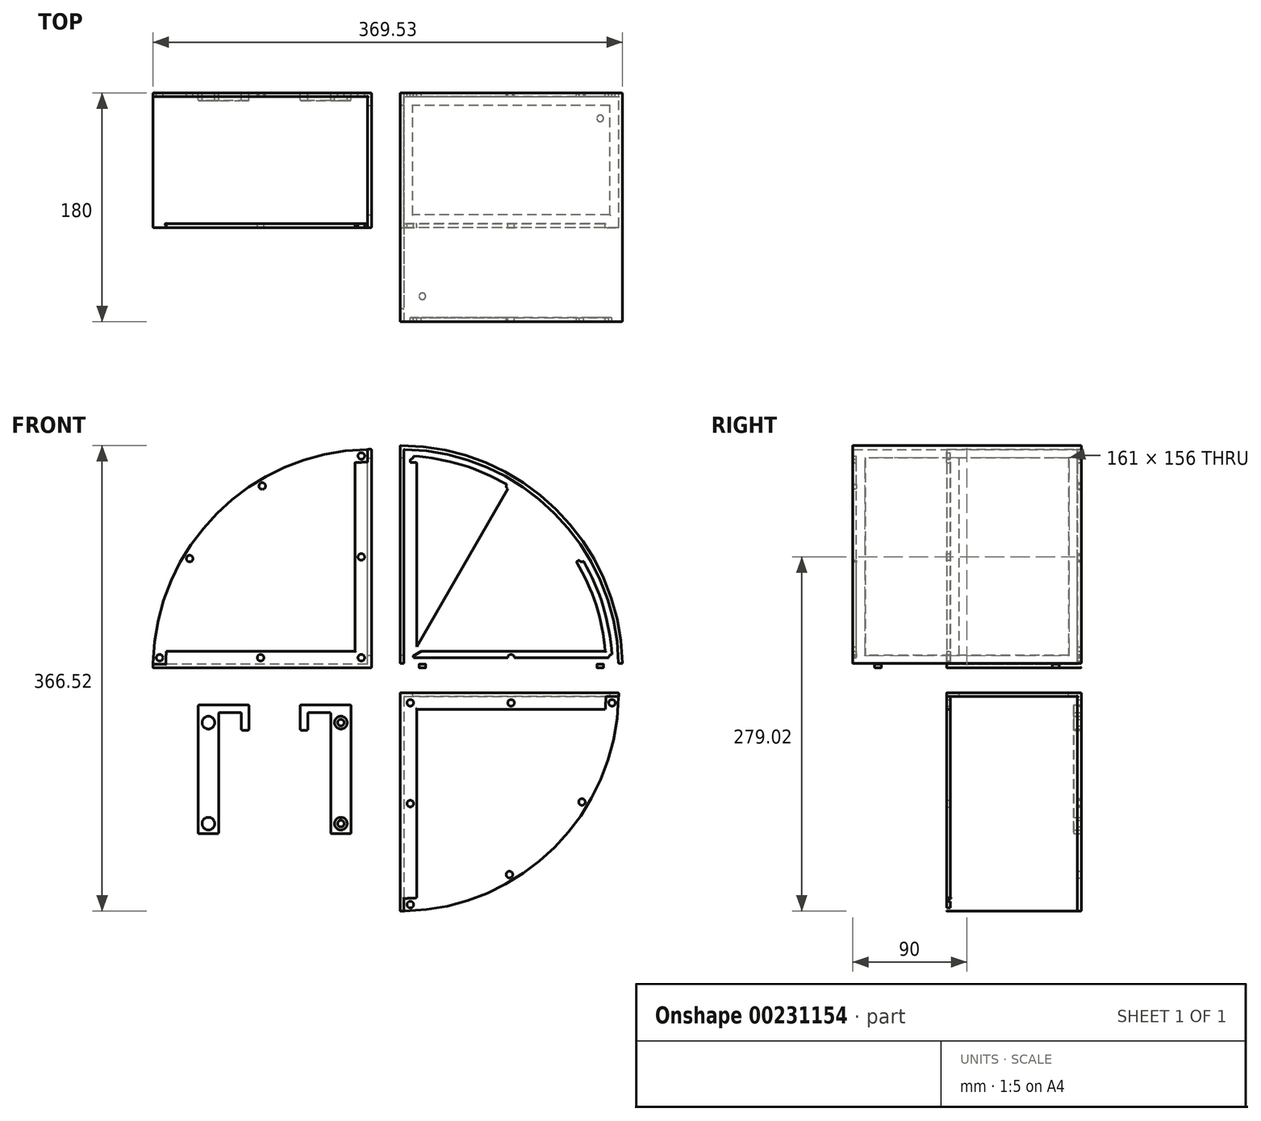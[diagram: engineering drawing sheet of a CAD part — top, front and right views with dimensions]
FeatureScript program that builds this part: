
annotation { "Feature Type Name" : "Feature", "Feature Type Description" : "" }
export const myFeature = defineFeature(function(context is Context, id is Id, definition is map)
    precondition{}
    {
        {
            var Q0;
            Q0=qCreatedBy(makeId("Front.planeOp"),FACE);
            var sketch = newSketch(context, id + "F0", { "sketchPlane" : qUnion([Q0])});
            skArc(sketch, "E0", {"start": v(186.3, 9.76) * mm, "mid": v(135.03, 133.5) * mm, "end": v(11.3, 184.76) * mm});
            skLineSegment(sketch, "E1", {"start": v(11.3, 184.76) * mm, "end": v(11.3, 9.76) * mm});
            skLineSegment(sketch, "E2", {"start": v(186.3, 9.76) * mm, "end": v(11.3, 9.76) * mm});
            skArc(sketch, "E3", {"start": v(11.3, 181.76) * mm, "mid": v(132.91, 131.38) * mm, "end": v(183.3, 9.76) * mm});
            skArc(sketch, "E4", {"start": v(11.3, 171.76) * mm, "mid": v(125.84, 124.31) * mm, "end": v(173.3, 9.76) * mm});
            skLineSegment(sketch, "E5", {"start": v(24.3, 22.76) * mm, "end": v(24.3, 171.24) * mm});
            skLineSegment(sketch, "E6", {"start": v(24.3, 171.24) * mm, "end": v(24.3, 22.76) * mm});
            skLineSegment(sketch, "E7", {"start": v(172.77, 22.76) * mm, "end": v(24.3, 22.76) * mm});
            skLineSegment(sketch, "E8", {"start": v(14.3, 12.76) * mm, "end": v(14.3, 181.73) * mm});
            skLineSegment(sketch, "E9", {"start": v(14.3, 12.76) * mm, "end": v(183.26, 12.76) * mm});
            skCircle(sketch, "E10", {"center": v(19.3, 17.76) * mm, "radius": 2.6 * mm});
            skArc(sketch, "E11", {"start": v(11.3, 176.76) * mm, "mid": v(129.38, 127.85) * mm, "end": v(178.3, 9.76) * mm});
            skCircle(sketch, "E12", {"center": v(19.3, 176.57) * mm, "radius": 2.6 * mm});
            skCircle(sketch, "E13", {"center": v(19.3, 97.07) * mm, "radius": 2.6 * mm});
            skCircle(sketch, "E14", {"center": v(98.6, 17.76) * mm, "radius": 2.6 * mm});
            skCircle(sketch, "E15", {"center": v(178.1, 17.76) * mm, "radius": 2.6 * mm});
            skCircle(sketch, "E16", {"center": v(97.31, 152.9) * mm, "radius": 2.6 * mm});
            skCircle(sketch, "E17", {"center": v(154.43, 95.78) * mm, "radius": 2.6 * mm});
            skLineSegment(sketch, "E18", {"start": v(19.3, 17.76) * mm, "end": v(19.3, 176.57) * mm});
            skLineSegment(sketch, "E19", {"start": v(19.3, 17.76) * mm, "end": v(178.1, 17.76) * mm});
            skLineSegment(sketch, "E20", {"start": v(19.3, 17.76) * mm, "end": v(97.31, 152.9) * mm});
            skLineSegment(sketch, "E21", {"start": v(19.3, 17.76) * mm, "end": v(154.43, 95.78) * mm});
            skLineSegment(sketch, "E22", {"start": v(0, 75.02) * mm, "end": v(0, -75.22) * mm});
            skLineSegment(sketch, "E23", {"start": v(-75, 0) * mm, "end": v(75.52, 0) * mm});
            skLineSegment(sketch, "E24.MirrorCS", {"start": v(186.3, -9.76) * mm, "end": v(11.3, -9.76) * mm});
            skLineSegment(sketch, "E25.MirrorCS", {"start": v(11.3, -184.76) * mm, "end": v(11.3, -9.76) * mm});
            skArc(sketch, "E26.MirrorCS", {"start": v(186.3, -9.76) * mm, "mid": v(135.03, -133.5) * mm, "end": v(11.3, -184.76) * mm});
            skArc(sketch, "E27.MirrorCS", {"start": v(11.3, -181.76) * mm, "mid": v(132.91, -131.38) * mm, "end": v(183.3, -9.76) * mm});
            skLineSegment(sketch, "E28.MirrorCS", {"start": v(14.3, -12.76) * mm, "end": v(14.3, -181.73) * mm});
            skLineSegment(sketch, "E29.MirrorCS", {"start": v(14.3, -12.76) * mm, "end": v(183.26, -12.76) * mm});
            skLineSegment(sketch, "E30.MirrorCS", {"start": v(172.77, -22.76) * mm, "end": v(24.3, -22.76) * mm});
            skLineSegment(sketch, "E31.MirrorCS", {"start": v(24.3, -171.24) * mm, "end": v(24.3, -22.76) * mm});
            skArc(sketch, "E32.MirrorCS", {"start": v(11.3, -171.76) * mm, "mid": v(125.84, -124.31) * mm, "end": v(173.3, -9.76) * mm});
            skCircle(sketch, "E33.MirrorC", {"center": v(19.3, -17.76) * mm, "radius": 2.6 * mm});
            skCircle(sketch, "E34.MirrorC", {"center": v(19.3, -97.07) * mm, "radius": 2.6 * mm});
            skCircle(sketch, "E35.MirrorC", {"center": v(19.3, -176.57) * mm, "radius": 2.6 * mm});
            skCircle(sketch, "E36.MirrorC", {"center": v(97.31, -152.9) * mm, "radius": 2.6 * mm});
            skCircle(sketch, "E37.MirrorC", {"center": v(154.43, -95.78) * mm, "radius": 2.6 * mm});
            skCircle(sketch, "E38.MirrorC", {"center": v(178.1, -17.76) * mm, "radius": 2.6 * mm});
            skCircle(sketch, "E39.MirrorC", {"center": v(98.6, -17.76) * mm, "radius": 2.6 * mm});
            skArc(sketch, "E40.MirrorCS", {"start": v(-186.3, 9.76) * mm, "mid": v(-135.03, 133.5) * mm, "end": v(-11.3, 184.76) * mm});
            skArc(sketch, "E41.MirrorCS", {"start": v(-11.3, 181.76) * mm, "mid": v(-132.91, 131.38) * mm, "end": v(-183.3, 9.76) * mm});
            skArc(sketch, "E42.MirrorCS", {"start": v(-11.3, 171.76) * mm, "mid": v(-125.84, 124.31) * mm, "end": v(-173.3, 9.76) * mm});
            skLineSegment(sketch, "E43.MirrorCS", {"start": v(-11.3, 184.76) * mm, "end": v(-11.3, 9.76) * mm});
            skLineSegment(sketch, "E44.MirrorCS", {"start": v(-14.3, 12.76) * mm, "end": v(-14.3, 181.73) * mm});
            skLineSegment(sketch, "E45.MirrorCS", {"start": v(-24.3, 171.24) * mm, "end": v(-24.3, 22.76) * mm});
            skLineSegment(sketch, "E46.MirrorCS", {"start": v(-172.77, 22.76) * mm, "end": v(-24.3, 22.76) * mm});
            skLineSegment(sketch, "E47.MirrorCS", {"start": v(-14.3, 12.76) * mm, "end": v(-183.26, 12.76) * mm});
            skLineSegment(sketch, "E48.MirrorCS", {"start": v(-186.3, 9.76) * mm, "end": v(-11.3, 9.76) * mm});
            skCircle(sketch, "E49.MirrorC", {"center": v(-19.3, 176.57) * mm, "radius": 2.6 * mm});
            skCircle(sketch, "E50.MirrorC", {"center": v(-97.31, 152.9) * mm, "radius": 2.6 * mm});
            skCircle(sketch, "E51.MirrorC", {"center": v(-154.43, 95.78) * mm, "radius": 2.6 * mm});
            skCircle(sketch, "E52.MirrorC", {"center": v(-178.1, 17.76) * mm, "radius": 2.6 * mm});
            skCircle(sketch, "E53.MirrorC", {"center": v(-98.6, 17.76) * mm, "radius": 2.6 * mm});
            skCircle(sketch, "E54.MirrorC", {"center": v(-19.3, 17.76) * mm, "radius": 2.6 * mm});
            skCircle(sketch, "E55.MirrorC", {"center": v(-19.3, 97.07) * mm, "radius": 2.6 * mm});
            skLineSegment(sketch, "E56", {"start": v(-27.37, -19.33) * mm, "end": v(-27.37, -120.83) * mm});
            skLineSegment(sketch, "E57", {"start": v(-27.37, -120.83) * mm, "end": v(-43.37, -120.83) * mm});
            skLineSegment(sketch, "E58", {"start": v(-43.37, -120.83) * mm, "end": v(-43.37, -25.33) * mm});
            skLineSegment(sketch, "E59", {"start": v(-43.37, -25.33) * mm, "end": v(-61.37, -25.33) * mm});
            skLineSegment(sketch, "E60", {"start": v(-61.37, -25.33) * mm, "end": v(-61.37, -39.33) * mm});
            skLineSegment(sketch, "E61", {"start": v(-61.37, -39.33) * mm, "end": v(-67.37, -39.33) * mm});
            skLineSegment(sketch, "E62", {"start": v(-67.37, -39.33) * mm, "end": v(-67.37, -19.33) * mm});
            skLineSegment(sketch, "E63", {"start": v(-67.37, -19.33) * mm, "end": v(-27.37, -19.33) * mm});
            skCircle(sketch, "E64", {"center": v(-35.37, -33.33) * mm, "radius": 2.6 * mm});
            skCircle(sketch, "E65", {"center": v(-35.37, -112.83) * mm, "radius": 2.6 * mm});
            skCircle(sketch, "E66", {"center": v(-35.37, -33.33) * mm, "radius": 5 * mm});
            skCircle(sketch, "E67", {"center": v(-35.37, -112.83) * mm, "radius": 5 * mm});
            skLineSegment(sketch, "E68", {"start": v(-87.52, -13.83) * mm, "end": v(-87.52, -51.3) * mm});
            skLineSegment(sketch, "E69.MirrorCS", {"start": v(-107.67, -19.33) * mm, "end": v(-147.67, -19.33) * mm});
            skLineSegment(sketch, "E70.MirrorCS", {"start": v(-107.67, -39.33) * mm, "end": v(-107.67, -19.33) * mm});
            skLineSegment(sketch, "E71.MirrorCS", {"start": v(-113.67, -25.33) * mm, "end": v(-113.67, -39.33) * mm});
            skLineSegment(sketch, "E72.MirrorCS", {"start": v(-131.67, -25.33) * mm, "end": v(-113.67, -25.33) * mm});
            skLineSegment(sketch, "E73.MirrorCS", {"start": v(-113.67, -39.33) * mm, "end": v(-107.67, -39.33) * mm});
            skLineSegment(sketch, "E74.MirrorCS", {"start": v(-131.67, -120.83) * mm, "end": v(-131.67, -25.33) * mm});
            skLineSegment(sketch, "E75.MirrorCS", {"start": v(-147.67, -120.83) * mm, "end": v(-131.67, -120.83) * mm});
            skLineSegment(sketch, "E76.MirrorCS", {"start": v(-147.67, -19.33) * mm, "end": v(-147.67, -120.83) * mm});
            skCircle(sketch, "E77.MirrorC", {"center": v(-139.67, -33.33) * mm, "radius": 5 * mm});
            skCircle(sketch, "E78.MirrorC", {"center": v(-139.67, -33.33) * mm, "radius": 2.6 * mm});
            skCircle(sketch, "E79.MirrorC", {"center": v(-139.67, -112.83) * mm, "radius": 5 * mm});
            skCircle(sketch, "E80.MirrorC", {"center": v(-139.67, -112.83) * mm, "radius": 2.6 * mm});
            skSolve(sketch);
        }
        {
            var Q0;
            {var subQ4=sQuery(id+"F0.wireOp",EDGE,"E0");Q0=makeQuery(id+"F0.imprint","IMPRINT",FACE,{"disambiguationData":[TD([[makeQuery(id+"F0.imprint","IMPRINT",EDGE,{"derivedFrom":subQ4}),1.0]])]});}
            var Q1;
            {var subQ1=sQuery(id+"F0.wireOp",EDGE,"E2");var subQ5=sQuery(id+"F0.wireOp",EDGE,"E1");var subQ9=makeQuery(id+"F0.imprint","INTERSECT",VERTEX,{"derivedFrom":[subQ5,subQ1]});Q1=makeQuery(id+"F0.imprint","IMPRINT",FACE,{"disambiguationData":[TD([[makeQuery(id+"F0.imprint","IMPRINT",EDGE,{"disambiguationData":[TD([[subQ9,1.0]])],"derivedFrom":subQ5}),1.0]])]});}
            var Q2;
            {var subQ0=sQuery(id+"F0.wireOp",EDGE,"E3");var subQ1=sQuery(id+"F0.wireOp",EDGE,"E2");var subQ2=makeQuery(id+"F0.imprint","INTERSECT",VERTEX,{"derivedFrom":[subQ1,subQ0]});Q2=makeQuery(id+"F0.imprint","IMPRINT",FACE,{"disambiguationData":[TD([[makeQuery(id+"F0.imprint","IMPRINT",EDGE,{"disambiguationData":[TD([[subQ2,-1.0]])],"derivedFrom":subQ1}),-1.0]])]});}
            var Q3;
            {var subQ0=sQuery(id+"F0.wireOp",EDGE,"E4");var subQ1=sQuery(id+"F0.wireOp",EDGE,"E2");var subQ2=makeQuery(id+"F0.imprint","INTERSECT",VERTEX,{"derivedFrom":[subQ1,subQ0]});Q3=makeQuery(id+"F0.imprint","IMPRINT",FACE,{"disambiguationData":[TD([[makeQuery(id+"F0.imprint","IMPRINT",EDGE,{"disambiguationData":[TD([[subQ2,1.0]])],"derivedFrom":subQ1}),-1.0]])]});}
            var Q4;
            {var subQ0=sQuery(id+"F0.wireOp",EDGE,"E3");var subQ1=sQuery(id+"F0.wireOp",EDGE,"E1");var subQ2=makeQuery(id+"F0.imprint","INTERSECT",VERTEX,{"derivedFrom":[subQ1,subQ0]});Q4=makeQuery(id+"F0.imprint","IMPRINT",FACE,{"disambiguationData":[TD([[makeQuery(id+"F0.imprint","IMPRINT",EDGE,{"disambiguationData":[TD([[subQ2,-1.0]])],"derivedFrom":subQ1}),1.0]])]});}
            var Q5;
            {var subQ0=sQuery(id+"F0.wireOp",EDGE,"E4");var subQ1=sQuery(id+"F0.wireOp",EDGE,"E1");var subQ2=makeQuery(id+"F0.imprint","INTERSECT",VERTEX,{"derivedFrom":[subQ1,subQ0]});Q5=makeQuery(id+"F0.imprint","IMPRINT",FACE,{"disambiguationData":[TD([[makeQuery(id+"F0.imprint","IMPRINT",EDGE,{"disambiguationData":[TD([[subQ2,1.0]])],"derivedFrom":subQ1}),1.0]])]});}
            extrude(context, id + "F1", {"entities" : qUnion([Q0, Q1, Q2, Q3, Q4, Q5]), "depth" : 180 * mm});
        }
        {
            var Q0;
            {var subQ4=sQuery(id+"F0.wireOp",EDGE,"E8");var subQ17=sQuery(id+"F0.wireOp",EDGE,"E3");var subQ18=makeQuery(id+"F0.imprint","INTERSECT",VERTEX,{"derivedFrom":[subQ17,subQ4]});Q0=makeQuery(id+"F0.imprint","IMPRINT",FACE,{"disambiguationData":[TD([[makeQuery(id+"F0.imprint","IMPRINT",EDGE,{"disambiguationData":[TD([[subQ18,-1.0]])],"derivedFrom":subQ17}),-1.0]])]});}
            var Q1;
            {var subQ5=sQuery(id+"F0.wireOp",EDGE,"E4");var subQ6=makeQuery(id+"F0.imprint","INTERSECT",VERTEX,{"derivedFrom":[subQ5,sQuery(id+"F0.wireOp",EDGE,"E7")]});Q1=makeQuery(id+"F0.imprint","IMPRINT",FACE,{"disambiguationData":[TD([[makeQuery(id+"F0.imprint","IMPRINT",EDGE,{"disambiguationData":[TD([[subQ6,1.0]])],"derivedFrom":subQ5}),1.0]])]});}
            var Q2;
            {var subQ3=sQuery(id+"F0.wireOp",EDGE,"E19");var subQ7=sQuery(id+"F0.wireOp",EDGE,"E4");var subQ9=makeQuery(id+"F0.imprint","INTERSECT",VERTEX,{"derivedFrom":[subQ7,subQ3]});Q2=makeQuery(id+"F0.imprint","IMPRINT",FACE,{"disambiguationData":[TD([[makeQuery(id+"F0.imprint","IMPRINT",EDGE,{"disambiguationData":[TD([[subQ9,-1.0]])],"derivedFrom":subQ7}),1.0]])]});}
            var Q3;
            {var subQ11=sQuery(id+"F0.wireOp",EDGE,"E8");var subQ12=sQuery(id+"F0.wireOp",EDGE,"E4");var subQ13=makeQuery(id+"F0.imprint","INTERSECT",VERTEX,{"derivedFrom":[subQ12,subQ11]});Q3=makeQuery(id+"F0.imprint","IMPRINT",FACE,{"disambiguationData":[TD([[makeQuery(id+"F0.imprint","IMPRINT",EDGE,{"disambiguationData":[TD([[subQ13,-1.0]])],"derivedFrom":subQ12}),-1.0]])]});}
            var Q4;
            {var subQ8=sQuery(id+"F0.wireOp",EDGE,"E4");var subQ10=sQuery(id+"F0.wireOp",EDGE,"E7");var subQ11=makeQuery(id+"F0.imprint","INTERSECT",VERTEX,{"derivedFrom":[subQ8,subQ10]});Q4=makeQuery(id+"F0.imprint","IMPRINT",FACE,{"disambiguationData":[TD([[makeQuery(id+"F0.imprint","IMPRINT",EDGE,{"disambiguationData":[TD([[subQ11,-1.0]])],"derivedFrom":subQ8}),-1.0]])]});}
            var Q5;
            {var subQ1=sQuery(id+"F0.wireOp",EDGE,"E6");var subQ5=sQuery(id+"F0.wireOp",EDGE,"E7");var subQ6=makeQuery(id+"F0.imprint","INTERSECT",VERTEX,{"derivedFrom":[subQ1,subQ5]});Q5=makeQuery(id+"F0.imprint","IMPRINT",FACE,{"disambiguationData":[TD([[makeQuery(id+"F0.imprint","IMPRINT",EDGE,{"disambiguationData":[TD([[subQ6,1.0]])],"derivedFrom":subQ1}),-1.0]])]});}
            var Q6;
            {var subQ5=sQuery(id+"F0.wireOp",EDGE,"E6");var subQ6=sQuery(id+"F0.wireOp",EDGE,"E4");var subQ7=makeQuery(id+"F0.imprint","INTERSECT",VERTEX,{"derivedFrom":[subQ6,subQ5]});Q6=makeQuery(id+"F0.imprint","IMPRINT",FACE,{"disambiguationData":[TD([[makeQuery(id+"F0.imprint","IMPRINT",EDGE,{"disambiguationData":[TD([[subQ7,1.0]])],"derivedFrom":subQ6}),-1.0]])]});}
            var Q7;
            {var subQ7=sQuery(id+"F0.wireOp",EDGE,"E4");var subQ9=sQuery(id+"F0.wireOp",EDGE,"E20");var subQ11=makeQuery(id+"F0.imprint","INTERSECT",VERTEX,{"derivedFrom":[subQ7,subQ9]});Q7=makeQuery(id+"F0.imprint","IMPRINT",FACE,{"disambiguationData":[TD([[makeQuery(id+"F0.imprint","IMPRINT",EDGE,{"disambiguationData":[TD([[subQ11,-1.0]])],"derivedFrom":subQ7}),1.0]])]});}
            var Q8;
            {var subQ5=sQuery(id+"F0.wireOp",EDGE,"E8");var subQ7=sQuery(id+"F0.wireOp",EDGE,"E4");var subQ8=makeQuery(id+"F0.imprint","INTERSECT",VERTEX,{"derivedFrom":[subQ7,subQ5]});Q8=makeQuery(id+"F0.imprint","IMPRINT",FACE,{"disambiguationData":[TD([[makeQuery(id+"F0.imprint","IMPRINT",EDGE,{"disambiguationData":[TD([[subQ8,-1.0]])],"derivedFrom":subQ7}),1.0]])]});}
            var Q9;
            {var subQ5=sQuery(id+"F0.wireOp",EDGE,"E4");var subQ6=makeQuery(id+"F0.imprint","INTERSECT",VERTEX,{"derivedFrom":[subQ5,sQuery(id+"F0.wireOp",EDGE,"E6")]});Q9=makeQuery(id+"F0.imprint","IMPRINT",FACE,{"disambiguationData":[TD([[makeQuery(id+"F0.imprint","IMPRINT",EDGE,{"disambiguationData":[TD([[subQ6,1.0]])],"derivedFrom":subQ5}),1.0]])]});}
            extrude(context, id + "F2", {"entities" : qUnion([Q0, Q1, Q2, Q3, Q4, Q5, Q6, Q7, Q8, Q9]), "operationType" : NewBodyOperationType.ADD, "depth" : 180 * mm, "hasSecondDirection" : true, "secondDirectionOppositeDirection" : false, "secondDirectionDepth" : 177 * mm});
        }
        {
            var Q0;
            {var subQ8=sQuery(id+"F0.wireOp",EDGE,"E4");var subQ10=sQuery(id+"F0.wireOp",EDGE,"E7");var subQ11=makeQuery(id+"F0.imprint","INTERSECT",VERTEX,{"derivedFrom":[subQ8,subQ10]});Q0=makeQuery(id+"F0.imprint","IMPRINT",FACE,{"disambiguationData":[TD([[makeQuery(id+"F0.imprint","IMPRINT",EDGE,{"disambiguationData":[TD([[subQ11,-1.0]])],"derivedFrom":subQ8}),-1.0]])]});}
            var Q1;
            {var subQ11=sQuery(id+"F0.wireOp",EDGE,"E8");var subQ12=sQuery(id+"F0.wireOp",EDGE,"E4");var subQ13=makeQuery(id+"F0.imprint","INTERSECT",VERTEX,{"derivedFrom":[subQ12,subQ11]});Q1=makeQuery(id+"F0.imprint","IMPRINT",FACE,{"disambiguationData":[TD([[makeQuery(id+"F0.imprint","IMPRINT",EDGE,{"disambiguationData":[TD([[subQ13,-1.0]])],"derivedFrom":subQ12}),-1.0]])]});}
            var Q2;
            {var subQ1=sQuery(id+"F0.wireOp",EDGE,"E6");var subQ5=sQuery(id+"F0.wireOp",EDGE,"E7");var subQ6=makeQuery(id+"F0.imprint","INTERSECT",VERTEX,{"derivedFrom":[subQ1,subQ5]});Q2=makeQuery(id+"F0.imprint","IMPRINT",FACE,{"disambiguationData":[TD([[makeQuery(id+"F0.imprint","IMPRINT",EDGE,{"disambiguationData":[TD([[subQ6,1.0]])],"derivedFrom":subQ1}),-1.0]])]});}
            var Q3;
            {var subQ5=sQuery(id+"F0.wireOp",EDGE,"E6");var subQ6=sQuery(id+"F0.wireOp",EDGE,"E4");var subQ7=makeQuery(id+"F0.imprint","INTERSECT",VERTEX,{"derivedFrom":[subQ6,subQ5]});Q3=makeQuery(id+"F0.imprint","IMPRINT",FACE,{"disambiguationData":[TD([[makeQuery(id+"F0.imprint","IMPRINT",EDGE,{"disambiguationData":[TD([[subQ7,1.0]])],"derivedFrom":subQ6}),-1.0]])]});}
            var Q4;
            {var subQ3=sQuery(id+"F0.wireOp",EDGE,"E19");var subQ7=sQuery(id+"F0.wireOp",EDGE,"E4");var subQ9=makeQuery(id+"F0.imprint","INTERSECT",VERTEX,{"derivedFrom":[subQ7,subQ3]});Q4=makeQuery(id+"F0.imprint","IMPRINT",FACE,{"disambiguationData":[TD([[makeQuery(id+"F0.imprint","IMPRINT",EDGE,{"disambiguationData":[TD([[subQ9,-1.0]])],"derivedFrom":subQ7}),1.0]])]});}
            var Q5;
            {var subQ4=sQuery(id+"F0.wireOp",EDGE,"E8");var subQ17=sQuery(id+"F0.wireOp",EDGE,"E3");var subQ18=makeQuery(id+"F0.imprint","INTERSECT",VERTEX,{"derivedFrom":[subQ17,subQ4]});Q5=makeQuery(id+"F0.imprint","IMPRINT",FACE,{"disambiguationData":[TD([[makeQuery(id+"F0.imprint","IMPRINT",EDGE,{"disambiguationData":[TD([[subQ18,-1.0]])],"derivedFrom":subQ17}),-1.0]])]});}
            var Q6;
            {var subQ5=sQuery(id+"F0.wireOp",EDGE,"E4");var subQ6=makeQuery(id+"F0.imprint","INTERSECT",VERTEX,{"derivedFrom":[subQ5,sQuery(id+"F0.wireOp",EDGE,"E7")]});Q6=makeQuery(id+"F0.imprint","IMPRINT",FACE,{"disambiguationData":[TD([[makeQuery(id+"F0.imprint","IMPRINT",EDGE,{"disambiguationData":[TD([[subQ6,1.0]])],"derivedFrom":subQ5}),1.0]])]});}
            var Q7;
            {var subQ7=sQuery(id+"F0.wireOp",EDGE,"E4");var subQ9=sQuery(id+"F0.wireOp",EDGE,"E20");var subQ11=makeQuery(id+"F0.imprint","INTERSECT",VERTEX,{"derivedFrom":[subQ7,subQ9]});Q7=makeQuery(id+"F0.imprint","IMPRINT",FACE,{"disambiguationData":[TD([[makeQuery(id+"F0.imprint","IMPRINT",EDGE,{"disambiguationData":[TD([[subQ11,-1.0]])],"derivedFrom":subQ7}),1.0]])]});}
            var Q8;
            {var subQ5=sQuery(id+"F0.wireOp",EDGE,"E8");var subQ7=sQuery(id+"F0.wireOp",EDGE,"E4");var subQ8=makeQuery(id+"F0.imprint","INTERSECT",VERTEX,{"derivedFrom":[subQ7,subQ5]});Q8=makeQuery(id+"F0.imprint","IMPRINT",FACE,{"disambiguationData":[TD([[makeQuery(id+"F0.imprint","IMPRINT",EDGE,{"disambiguationData":[TD([[subQ8,-1.0]])],"derivedFrom":subQ7}),1.0]])]});}
            var Q9;
            {var subQ5=sQuery(id+"F0.wireOp",EDGE,"E4");var subQ6=makeQuery(id+"F0.imprint","INTERSECT",VERTEX,{"derivedFrom":[subQ5,sQuery(id+"F0.wireOp",EDGE,"E6")]});Q9=makeQuery(id+"F0.imprint","IMPRINT",FACE,{"disambiguationData":[TD([[makeQuery(id+"F0.imprint","IMPRINT",EDGE,{"disambiguationData":[TD([[subQ6,1.0]])],"derivedFrom":subQ5}),1.0]])]});}
            extrude(context, id + "F3", {"entities" : qUnion([Q0, Q1, Q2, Q3, Q4, Q5, Q6, Q7, Q8, Q9]), "operationType" : NewBodyOperationType.ADD, "depth" : 3 * mm});
        }
        {
            var Q0;
            Q0=makeQuery(id+"F1.opExtrude","SWEPT_FACE",FACE,{"disambiguationData":[OSD([sQuery(id+"F0.wireOp",EDGE,"E2")])]});
            var sketch = newSketch(context, id + "F4", { "sketchPlane" : qUnion([Q0])});
            skCircle(sketch, "E81", {"center": v(98.8, 90) * mm, "radius": 80 * mm});
            skLineSegment(sketch, "E82", {"start": v(98.8, 90) * mm, "end": v(98.8, 60.24) * mm});
            skLineSegment(sketch, "E83", {"start": v(98.8, 90) * mm, "end": v(64.71, 90) * mm});
            skCircle(sketch, "E84", {"center": v(168.8, 160) * mm, "radius": 2.6 * mm});
            skCircle(sketch, "E85.MirrorC", {"center": v(168.8, 20) * mm, "radius": 2.6 * mm});
            skCircle(sketch, "E86.MirrorC", {"center": v(28.8, 160) * mm, "radius": 2.6 * mm});
            skCircle(sketch, "E87.MirrorC", {"center": v(28.8, 20) * mm, "radius": 2.6 * mm});
            skSolve(sketch);
        }
        {
            var Q0;
            Q0=makeQuery(id+"F4.imprint","IMPRINT",FACE,{"disambiguationData":[TD([[makeQuery(id+"F4.imprint","IMPRINT",EDGE,{"derivedFrom":sQuery(id+"F4.wireOp",EDGE,"E84")}),1.0]])]});
            var Q1;
            Q1=makeQuery(id+"F4.imprint","IMPRINT",FACE,{"disambiguationData":[TD([[makeQuery(id+"F4.imprint","IMPRINT",EDGE,{"derivedFrom":sQuery(id+"F4.wireOp",EDGE,"E85.MirrorC")}),-1.0]])]});
            var Q2;
            Q2=makeQuery(id+"F4.imprint","IMPRINT",FACE,{"disambiguationData":[TD([[makeQuery(id+"F4.imprint","IMPRINT",EDGE,{"derivedFrom":sQuery(id+"F4.wireOp",EDGE,"E86.MirrorC")}),-1.0]])]});
            var Q3;
            Q3=makeQuery(id+"F4.imprint","IMPRINT",FACE,{"disambiguationData":[TD([[makeQuery(id+"F4.imprint","IMPRINT",EDGE,{"derivedFrom":sQuery(id+"F4.wireOp",EDGE,"E87.MirrorC")}),1.0]])]});
            var Q4;
            Q4=makeQuery(id+"F4.imprint","IMPRINT",FACE,{"disambiguationData":[TD([[makeQuery(id+"F4.imprint","IMPRINT",EDGE,{"derivedFrom":sQuery(id+"F4.wireOp",EDGE,"E81")}),1.0]])]});
            extrude(context, id + "F5", {"entities" : qUnion([Q0, Q1, Q2, Q3, Q4]), "operationType" : NewBodyOperationType.REMOVE, "oppositeDirection" : true, "depth" : 3.5 * mm});
        }
        {
            var Q0;
            Q0=makeQuery(id+"F1.opExtrude","SWEPT_FACE",FACE,{"disambiguationData":[OSD([sQuery(id+"F0.wireOp",EDGE,"E1")])]});
            var sketch = newSketch(context, id + "F6", { "sketchPlane" : qUnion([Q0])});
            skLineSegment(sketch, "E88.bottom", {"start": v(10, 174.76) * mm, "end": v(170, 174.76) * mm});
            skLineSegment(sketch, "E88.top", {"start": v(10, 19.76) * mm, "end": v(170, 19.76) * mm});
            skLineSegment(sketch, "E88.left", {"start": v(10, 174.76) * mm, "end": v(10, 19.76) * mm});
            skLineSegment(sketch, "E88.right", {"start": v(170, 174.76) * mm, "end": v(170, 19.76) * mm});
            skSolve(sketch);
        }
        {
            var Q0;
            Q0=makeQuery(id+"F6.imprint","IMPRINT",FACE,{"disambiguationData":[TD([[makeQuery(id+"F6.imprint","IMPRINT",EDGE,{"derivedFrom":sQuery(id+"F6.wireOp",EDGE,"E88.bottom")}),-1.0]])]});
            extrude(context, id + "F7", {"entities" : qUnion([Q0]), "operationType" : NewBodyOperationType.REMOVE, "oppositeDirection" : true, "depth" : 3.5 * mm});
        }
        {
            var Q0;
            Q0=makeQuery(id+"F0.imprint","IMPRINT",FACE,{"disambiguationData":[TD([[makeQuery(id+"F0.imprint","IMPRINT",EDGE,{"derivedFrom":sQuery(id+"F0.wireOp",EDGE,"E56")}),-1.0]])]});
            var Q1;
            Q1=makeQuery(id+"F0.imprint","IMPRINT",FACE,{"disambiguationData":[TD([[makeQuery(id+"F0.imprint","IMPRINT",EDGE,{"derivedFrom":sQuery(id+"F0.wireOp",EDGE,"E69.MirrorCS")}),1.0]])]});
            extrude(context, id + "F8", {"entities" : qUnion([Q0, Q1]), "depth" : 6 * mm});
        }
        {
            var Q0;
            Q0=makeQuery(id+"F0.imprint","IMPRINT",FACE,{"disambiguationData":[TD([[makeQuery(id+"F0.imprint","IMPRINT",EDGE,{"derivedFrom":sQuery(id+"F0.wireOp",EDGE,"E64")}),-1.0]])]});
            var Q1;
            Q1=makeQuery(id+"F0.imprint","IMPRINT",FACE,{"disambiguationData":[TD([[makeQuery(id+"F0.imprint","IMPRINT",EDGE,{"derivedFrom":sQuery(id+"F0.wireOp",EDGE,"E65")}),-1.0]])]});
            extrude(context, id + "F9", {"entities" : qUnion([Q0, Q1]), "operationType" : NewBodyOperationType.ADD, "depth" : 3 * mm});
        }
        {
            var Q0;
            Q0=makeQuery(id+"F0.imprint","IMPRINT",FACE,{"disambiguationData":[TD([[makeQuery(id+"F0.imprint","IMPRINT",EDGE,{"derivedFrom":sQuery(id+"F0.wireOp",EDGE,"E79.MirrorC")}),-1.0]])]});
            var Q1;
            Q1=makeQuery(id+"F0.imprint","IMPRINT",FACE,{"disambiguationData":[TD([[makeQuery(id+"F0.imprint","IMPRINT",EDGE,{"derivedFrom":sQuery(id+"F0.wireOp",EDGE,"E77.MirrorC")}),-1.0]])]});
            extrude(context, id + "F10", {"entities" : qUnion([Q0, Q1]), "operationType" : NewBodyOperationType.ADD, "depth" : 3 * mm});
        }
        {
            var Q0;
            {var subQ3=sQuery(id+"F0.wireOp",EDGE,"E42.MirrorCS");var subQ5=sQuery(id+"F0.wireOp",EDGE,"E43.MirrorCS");var subQ6=makeQuery(id+"F0.imprint","INTERSECT",VERTEX,{"derivedFrom":[subQ3,subQ5]});Q0=makeQuery(id+"F0.imprint","IMPRINT",FACE,{"disambiguationData":[TD([[makeQuery(id+"F0.imprint","IMPRINT",EDGE,{"disambiguationData":[TD([[subQ6,-1.0]])],"derivedFrom":subQ3}),1.0]])]});}
            var Q1;
            {var subQ0=sQuery(id+"F0.wireOp",EDGE,"E48.MirrorCS");var subQ1=sQuery(id+"F0.wireOp",EDGE,"E41.MirrorCS");var subQ2=makeQuery(id+"F0.imprint","INTERSECT",VERTEX,{"derivedFrom":[subQ1,subQ0]});Q1=makeQuery(id+"F0.imprint","IMPRINT",FACE,{"disambiguationData":[TD([[makeQuery(id+"F0.imprint","IMPRINT",EDGE,{"disambiguationData":[TD([[subQ2,1.0]])],"derivedFrom":subQ1}),1.0]])]});}
            var Q2;
            {var subQ0=sQuery(id+"F0.wireOp",EDGE,"E43.MirrorCS");var subQ1=sQuery(id+"F0.wireOp",EDGE,"E41.MirrorCS");var subQ2=makeQuery(id+"F0.imprint","INTERSECT",VERTEX,{"derivedFrom":[subQ1,subQ0]});Q2=makeQuery(id+"F0.imprint","IMPRINT",FACE,{"disambiguationData":[TD([[makeQuery(id+"F0.imprint","IMPRINT",EDGE,{"disambiguationData":[TD([[subQ2,-1.0]])],"derivedFrom":subQ1}),1.0]])]});}
            var Q3;
            {var subQ7=sQuery(id+"F0.wireOp",EDGE,"E40.MirrorCS");Q3=makeQuery(id+"F0.imprint","IMPRINT",FACE,{"disambiguationData":[TD([[makeQuery(id+"F0.imprint","IMPRINT",EDGE,{"derivedFrom":subQ7}),-1.0]])]});}
            extrude(context, id + "F11", {"entities" : qUnion([Q0, Q1, Q2, Q3]), "depth" : 106 * mm});
        }
        {
            var Q0;
            {var subQ0=sQuery(id+"F0.wireOp",EDGE,"E45.MirrorCS");Q0=makeQuery(id+"F0.imprint","IMPRINT",FACE,{"disambiguationData":[TD([[makeQuery(id+"F0.imprint","IMPRINT",EDGE,{"derivedFrom":subQ0}),1.0]])]});}
            var Q1;
            Q1=makeQuery(id+"F0.imprint","IMPRINT",FACE,{"disambiguationData":[TD([[makeQuery(id+"F0.imprint","IMPRINT",EDGE,{"derivedFrom":sQuery(id+"F0.wireOp",EDGE,"E49.MirrorC")}),1.0]])]});
            extrude(context, id + "F12", {"entities" : qUnion([Q0, Q1]), "operationType" : NewBodyOperationType.ADD, "depth" : 106 * mm, "hasSecondDirection" : true, "secondDirectionOppositeDirection" : false, "secondDirectionDepth" : 103 * mm});
        }
        {
            var Q0;
            {var subQ0=sQuery(id+"F0.wireOp",EDGE,"E45.MirrorCS");Q0=makeQuery(id+"F0.imprint","IMPRINT",FACE,{"disambiguationData":[TD([[makeQuery(id+"F0.imprint","IMPRINT",EDGE,{"derivedFrom":subQ0}),1.0]])]});}
            var Q1;
            Q1=makeQuery(id+"F0.imprint","IMPRINT",FACE,{"disambiguationData":[TD([[makeQuery(id+"F0.imprint","IMPRINT",EDGE,{"derivedFrom":sQuery(id+"F0.wireOp",EDGE,"E49.MirrorC")}),1.0]])]});
            var Q2;
            {var subQ0=sQuery(id+"F0.wireOp",EDGE,"E45.MirrorCS");Q2=makeQuery(id+"F0.imprint","IMPRINT",FACE,{"disambiguationData":[TD([[makeQuery(id+"F0.imprint","IMPRINT",EDGE,{"derivedFrom":subQ0}),-1.0]])]});}
            var Q3;
            Q3=makeQuery(id+"F0.imprint","IMPRINT",FACE,{"disambiguationData":[TD([[makeQuery(id+"F0.imprint","IMPRINT",EDGE,{"derivedFrom":sQuery(id+"F0.wireOp",EDGE,"E53.MirrorC")}),-1.0]])]});
            var Q4;
            Q4=makeQuery(id+"F0.imprint","IMPRINT",FACE,{"disambiguationData":[TD([[makeQuery(id+"F0.imprint","IMPRINT",EDGE,{"derivedFrom":sQuery(id+"F0.wireOp",EDGE,"E52.MirrorC")}),-1.0]])]});
            var Q5;
            Q5=makeQuery(id+"F0.imprint","IMPRINT",FACE,{"disambiguationData":[TD([[makeQuery(id+"F0.imprint","IMPRINT",EDGE,{"derivedFrom":sQuery(id+"F0.wireOp",EDGE,"E54.MirrorC")}),-1.0]])]});
            var Q6;
            Q6=makeQuery(id+"F0.imprint","IMPRINT",FACE,{"disambiguationData":[TD([[makeQuery(id+"F0.imprint","IMPRINT",EDGE,{"derivedFrom":sQuery(id+"F0.wireOp",EDGE,"E50.MirrorC")}),-1.0]])]});
            var Q7;
            Q7=makeQuery(id+"F0.imprint","IMPRINT",FACE,{"disambiguationData":[TD([[makeQuery(id+"F0.imprint","IMPRINT",EDGE,{"derivedFrom":sQuery(id+"F0.wireOp",EDGE,"E51.MirrorC")}),-1.0]])]});
            extrude(context, id + "F13", {"entities" : qUnion([Q0, Q1, Q2, Q3, Q4, Q5, Q6, Q7]), "operationType" : NewBodyOperationType.ADD, "depth" : 3 * mm});
        }
        {
            var Q0;
            Q0=makeQuery(id+"F11.opExtrude","SWEPT_FACE",FACE,{"disambiguationData":[OSD([sQuery(id+"F0.wireOp",EDGE,"E43.MirrorCS")])]});
            var sketch = newSketch(context, id + "F14", { "sketchPlane" : qUnion([Q0])});
            skLineSegment(sketch, "E89.bottom", {"start": v(-96, 174.76) * mm, "end": v(-10, 174.76) * mm});
            skLineSegment(sketch, "E89.top", {"start": v(-96, 19.76) * mm, "end": v(-10, 19.76) * mm});
            skLineSegment(sketch, "E89.left", {"start": v(-96, 174.76) * mm, "end": v(-96, 19.76) * mm});
            skLineSegment(sketch, "E89.right", {"start": v(-10, 174.76) * mm, "end": v(-10, 19.76) * mm});
            skSolve(sketch);
        }
        {
            var Q0;
            Q0=makeQuery(id+"F14.imprint","IMPRINT",FACE,{"disambiguationData":[TD([[makeQuery(id+"F14.imprint","IMPRINT",EDGE,{"derivedFrom":sQuery(id+"F14.wireOp",EDGE,"E89.bottom")}),-1.0]])]});
            extrude(context, id + "F15", {"entities" : qUnion([Q0]), "operationType" : NewBodyOperationType.REMOVE, "oppositeDirection" : true, "depth" : 3.5 * mm});
        }
        {
            var Q0;
            {var subQ5=sQuery(id+"F0.wireOp",EDGE,"E25.MirrorCS");var subQ6=sQuery(id+"F0.wireOp",EDGE,"E24.MirrorCS");var subQ7=makeQuery(id+"F0.imprint","INTERSECT",VERTEX,{"derivedFrom":[subQ6,subQ5]});Q0=makeQuery(id+"F0.imprint","IMPRINT",FACE,{"disambiguationData":[TD([[makeQuery(id+"F0.imprint","IMPRINT",EDGE,{"disambiguationData":[TD([[subQ7,1.0]])],"derivedFrom":subQ6}),1.0]])]});}
            var Q1;
            {var subQ0=sQuery(id+"F0.wireOp",EDGE,"E27.MirrorCS");var subQ1=sQuery(id+"F0.wireOp",EDGE,"E24.MirrorCS");var subQ2=makeQuery(id+"F0.imprint","INTERSECT",VERTEX,{"derivedFrom":[subQ1,subQ0]});Q1=makeQuery(id+"F0.imprint","IMPRINT",FACE,{"disambiguationData":[TD([[makeQuery(id+"F0.imprint","IMPRINT",EDGE,{"disambiguationData":[TD([[subQ2,-1.0]])],"derivedFrom":subQ1}),1.0]])]});}
            var Q2;
            {var subQ4=sQuery(id+"F0.wireOp",EDGE,"E26.MirrorCS");Q2=makeQuery(id+"F0.imprint","IMPRINT",FACE,{"disambiguationData":[TD([[makeQuery(id+"F0.imprint","IMPRINT",EDGE,{"derivedFrom":subQ4}),-1.0]])]});}
            var Q3;
            {var subQ0=sQuery(id+"F0.wireOp",EDGE,"E27.MirrorCS");var subQ1=sQuery(id+"F0.wireOp",EDGE,"E25.MirrorCS");var subQ2=makeQuery(id+"F0.imprint","INTERSECT",VERTEX,{"derivedFrom":[subQ1,subQ0]});Q3=makeQuery(id+"F0.imprint","IMPRINT",FACE,{"disambiguationData":[TD([[makeQuery(id+"F0.imprint","IMPRINT",EDGE,{"disambiguationData":[TD([[subQ2,-1.0]])],"derivedFrom":subQ1}),-1.0]])]});}
            extrude(context, id + "F16", {"entities" : qUnion([Q0, Q1, Q2, Q3]), "depth" : 106 * mm});
        }
        {
            var Q0;
            {var subQ0=sQuery(id+"F0.wireOp",EDGE,"E30.MirrorCS");Q0=makeQuery(id+"F0.imprint","IMPRINT",FACE,{"disambiguationData":[TD([[makeQuery(id+"F0.imprint","IMPRINT",EDGE,{"derivedFrom":subQ0}),-1.0]])]});}
            var Q1;
            Q1=makeQuery(id+"F0.imprint","IMPRINT",FACE,{"disambiguationData":[TD([[makeQuery(id+"F0.imprint","IMPRINT",EDGE,{"derivedFrom":sQuery(id+"F0.wireOp",EDGE,"E35.MirrorC")}),1.0]])]});
            extrude(context, id + "F17", {"entities" : qUnion([Q0, Q1]), "operationType" : NewBodyOperationType.ADD, "depth" : 106 * mm, "hasSecondDirection" : true, "secondDirectionOppositeDirection" : false, "secondDirectionDepth" : 103 * mm});
        }
        {
            var Q0;
            {var subQ0=sQuery(id+"F0.wireOp",EDGE,"E30.MirrorCS");Q0=makeQuery(id+"F0.imprint","IMPRINT",FACE,{"disambiguationData":[TD([[makeQuery(id+"F0.imprint","IMPRINT",EDGE,{"derivedFrom":subQ0}),-1.0]])]});}
            var Q1;
            Q1=makeQuery(id+"F0.imprint","IMPRINT",FACE,{"disambiguationData":[TD([[makeQuery(id+"F0.imprint","IMPRINT",EDGE,{"derivedFrom":sQuery(id+"F0.wireOp",EDGE,"E33.MirrorC")}),-1.0]])]});
            var Q2;
            Q2=makeQuery(id+"F0.imprint","IMPRINT",FACE,{"disambiguationData":[TD([[makeQuery(id+"F0.imprint","IMPRINT",EDGE,{"derivedFrom":sQuery(id+"F0.wireOp",EDGE,"E34.MirrorC")}),-1.0]])]});
            var Q3;
            {var subQ0=sQuery(id+"F0.wireOp",EDGE,"E30.MirrorCS");Q3=makeQuery(id+"F0.imprint","IMPRINT",FACE,{"disambiguationData":[TD([[makeQuery(id+"F0.imprint","IMPRINT",EDGE,{"derivedFrom":subQ0}),1.0]])]});}
            var Q4;
            Q4=makeQuery(id+"F0.imprint","IMPRINT",FACE,{"disambiguationData":[TD([[makeQuery(id+"F0.imprint","IMPRINT",EDGE,{"derivedFrom":sQuery(id+"F0.wireOp",EDGE,"E35.MirrorC")}),1.0]])]});
            var Q5;
            Q5=makeQuery(id+"F0.imprint","IMPRINT",FACE,{"disambiguationData":[TD([[makeQuery(id+"F0.imprint","IMPRINT",EDGE,{"derivedFrom":sQuery(id+"F0.wireOp",EDGE,"E37.MirrorC")}),-1.0]])]});
            var Q6;
            Q6=makeQuery(id+"F0.imprint","IMPRINT",FACE,{"disambiguationData":[TD([[makeQuery(id+"F0.imprint","IMPRINT",EDGE,{"derivedFrom":sQuery(id+"F0.wireOp",EDGE,"E36.MirrorC")}),-1.0]])]});
            var Q7;
            Q7=makeQuery(id+"F0.imprint","IMPRINT",FACE,{"disambiguationData":[TD([[makeQuery(id+"F0.imprint","IMPRINT",EDGE,{"derivedFrom":sQuery(id+"F0.wireOp",EDGE,"E35.MirrorC")}),-1.0]])]});
            extrude(context, id + "F18", {"entities" : qUnion([Q0, Q1, Q2, Q3, Q4, Q5, Q6, Q7]), "operationType" : NewBodyOperationType.ADD, "depth" : 3 * mm});
        }
        {
            var Q0;
            Q0=makeQuery(id+"F16.opExtrude","SWEPT_FACE",FACE,{"disambiguationData":[OSD([sQuery(id+"F0.wireOp",EDGE,"E24.MirrorCS")])]});
            var sketch = newSketch(context, id + "F19", { "sketchPlane" : qUnion([Q0])});
            skLineSegment(sketch, "E90.bottom", {"start": v(176.3, -96) * mm, "end": v(21.3, -96) * mm});
            skLineSegment(sketch, "E90.top", {"start": v(176.3, -10) * mm, "end": v(21.3, -10) * mm});
            skLineSegment(sketch, "E90.left", {"start": v(176.3, -96) * mm, "end": v(176.3, -10) * mm});
            skLineSegment(sketch, "E90.right", {"start": v(21.3, -96) * mm, "end": v(21.3, -10) * mm});
            skSolve(sketch);
        }
        {
            var Q0;
            Q0 = qSketchRegion(id + "F19", true);
            extrude(context, id + "F20", {"entities" : qUnion([Q0]), "operationType" : NewBodyOperationType.REMOVE, "oppositeDirection" : true, "depth" : 3.5 * mm});
        }
        {
            var Q0;
            Q0=makeQuery(id+"F10.opExtrude","CAP_EDGE",EDGE,{"disambiguationData":[OSD([sQuery(id+"F0.wireOp",EDGE,"E78.MirrorC")])],"isStart":false});
            var Q1;
            Q1=makeQuery(id+"F8.opExtrude","CAP_EDGE",EDGE,{"disambiguationData":[OSD([sQuery(id+"F0.wireOp",EDGE,"E77.MirrorC")])],"isStart":false});
            var Q2;
            Q2=makeQuery(id+"F9.opExtrude","CAP_EDGE",EDGE,{"disambiguationData":[OSD([sQuery(id+"F0.wireOp",EDGE,"E64")])],"isStart":false});
            var Q3;
            Q3=makeQuery(id+"F8.opExtrude","CAP_EDGE",EDGE,{"disambiguationData":[OSD([sQuery(id+"F0.wireOp",EDGE,"E66")])],"isStart":false});
            var Q4;
            Q4=makeQuery(id+"F9.opExtrude","CAP_EDGE",EDGE,{"disambiguationData":[OSD([sQuery(id+"F0.wireOp",EDGE,"E64")])],"isStart":true});
            var Q5;
            Q5=makeQuery(id+"F10.opExtrude","CAP_EDGE",EDGE,{"disambiguationData":[OSD([sQuery(id+"F0.wireOp",EDGE,"E78.MirrorC")])],"isStart":true});
            var Q6;
            Q6=makeQuery(id+"F10.opExtrude","CAP_EDGE",EDGE,{"disambiguationData":[OSD([sQuery(id+"F0.wireOp",EDGE,"E80.MirrorC")])],"isStart":true});
            var Q7;
            Q7=makeQuery(id+"F8.opExtrude","CAP_EDGE",EDGE,{"disambiguationData":[OSD([sQuery(id+"F0.wireOp",EDGE,"E79.MirrorC")])],"isStart":false});
            var Q8;
            Q8=makeQuery(id+"F10.opExtrude","CAP_EDGE",EDGE,{"disambiguationData":[OSD([sQuery(id+"F0.wireOp",EDGE,"E80.MirrorC")])],"isStart":false});
            var Q9;
            Q9=makeQuery(id+"F10.opExtrude","CAP_EDGE",EDGE,{"disambiguationData":[OSD([sQuery(id+"F0.wireOp",EDGE,"E79.MirrorC")])],"isStart":false});
            var Q10;
            Q10=makeQuery(id+"F9.opExtrude","CAP_EDGE",EDGE,{"disambiguationData":[OSD([sQuery(id+"F0.wireOp",EDGE,"E65")])],"isStart":true});
            var Q11;
            Q11=makeQuery(id+"F9.opExtrude","CAP_EDGE",EDGE,{"disambiguationData":[OSD([sQuery(id+"F0.wireOp",EDGE,"E65")])],"isStart":false});
            var Q12;
            Q12=makeQuery(id+"F9.opExtrude","CAP_EDGE",EDGE,{"disambiguationData":[OSD([sQuery(id+"F0.wireOp",EDGE,"E67")])],"isStart":false});
            var Q13;
            Q13=makeQuery(id+"F8.opExtrude","CAP_EDGE",EDGE,{"disambiguationData":[OSD([sQuery(id+"F0.wireOp",EDGE,"E67")])],"isStart":false});
            var Q14;
            Q14=makeQuery(id+"F10.opExtrude","CAP_EDGE",EDGE,{"disambiguationData":[OSD([sQuery(id+"F0.wireOp",EDGE,"E77.MirrorC")])],"isStart":false});
            var Q15;
            Q15=makeQuery(id+"F9.opExtrude","CAP_EDGE",EDGE,{"disambiguationData":[OSD([sQuery(id+"F0.wireOp",EDGE,"E66")])],"isStart":false});
            fillet(context, id + "F21", {"entities" : qUnion([Q0, Q1, Q2, Q3, Q4, Q5, Q6, Q7, Q8, Q9, Q10, Q11, Q12, Q13, Q14, Q15]), "radius" : 0.5 * mm, "tangentPropagation" : true, "allowEdgeOverflow" : false});
        }
        {
            var Q0;
            Q0=makeQuery(id+"F8.opExtrude","SWEPT_EDGE",EDGE,{"disambiguationData":[OSD([sQuery(id+"F0.wireOp",EDGE,"E71.MirrorCS"),sQuery(id+"F0.wireOp",EDGE,"E72.MirrorCS")])]});
            var Q1;
            Q1=makeQuery(id+"F8.opExtrude","SWEPT_EDGE",EDGE,{"disambiguationData":[OSD([sQuery(id+"F0.wireOp",EDGE,"E71.MirrorCS"),sQuery(id+"F0.wireOp",EDGE,"E73.MirrorCS")])]});
            var Q2;
            Q2=makeQuery(id+"F8.opExtrude","SWEPT_EDGE",EDGE,{"disambiguationData":[OSD([sQuery(id+"F0.wireOp",EDGE,"E70.MirrorCS"),sQuery(id+"F0.wireOp",EDGE,"E73.MirrorCS")])]});
            var Q3;
            Q3=makeQuery(id+"F8.opExtrude","SWEPT_EDGE",EDGE,{"disambiguationData":[OSD([sQuery(id+"F0.wireOp",EDGE,"E69.MirrorCS"),sQuery(id+"F0.wireOp",EDGE,"E76.MirrorCS")])]});
            var Q4;
            Q4=makeQuery(id+"F8.opExtrude","SWEPT_EDGE",EDGE,{"disambiguationData":[OSD([sQuery(id+"F0.wireOp",EDGE,"E62"),sQuery(id+"F0.wireOp",EDGE,"E63")])]});
            var Q5;
            Q5=makeQuery(id+"F8.opExtrude","SWEPT_EDGE",EDGE,{"disambiguationData":[OSD([sQuery(id+"F0.wireOp",EDGE,"E61"),sQuery(id+"F0.wireOp",EDGE,"E62")])]});
            var Q6;
            Q6=makeQuery(id+"F8.opExtrude","SWEPT_EDGE",EDGE,{"disambiguationData":[OSD([sQuery(id+"F0.wireOp",EDGE,"E60"),sQuery(id+"F0.wireOp",EDGE,"E61")])]});
            var Q7;
            Q7=makeQuery(id+"F8.opExtrude","SWEPT_EDGE",EDGE,{"disambiguationData":[OSD([sQuery(id+"F0.wireOp",EDGE,"E58"),sQuery(id+"F0.wireOp",EDGE,"E59")])]});
            var Q8;
            Q8=makeQuery(id+"F8.opExtrude","SWEPT_EDGE",EDGE,{"disambiguationData":[OSD([sQuery(id+"F0.wireOp",EDGE,"E56"),sQuery(id+"F0.wireOp",EDGE,"E57")])]});
            var Q9;
            Q9=makeQuery(id+"F8.opExtrude","SWEPT_EDGE",EDGE,{"disambiguationData":[OSD([sQuery(id+"F0.wireOp",EDGE,"E57"),sQuery(id+"F0.wireOp",EDGE,"E58")])]});
            var Q10;
            Q10=makeQuery(id+"F8.opExtrude","SWEPT_EDGE",EDGE,{"disambiguationData":[OSD([sQuery(id+"F0.wireOp",EDGE,"E74.MirrorCS"),sQuery(id+"F0.wireOp",EDGE,"E75.MirrorCS")])]});
            var Q11;
            Q11=makeQuery(id+"F8.opExtrude","SWEPT_EDGE",EDGE,{"disambiguationData":[OSD([sQuery(id+"F0.wireOp",EDGE,"E75.MirrorCS"),sQuery(id+"F0.wireOp",EDGE,"E76.MirrorCS")])]});
            var Q12;
            Q12=makeQuery(id+"F8.opExtrude","SWEPT_EDGE",EDGE,{"disambiguationData":[OSD([sQuery(id+"F0.wireOp",EDGE,"E72.MirrorCS"),sQuery(id+"F0.wireOp",EDGE,"E74.MirrorCS")])]});
            var Q13;
            Q13=makeQuery(id+"F8.opExtrude","SWEPT_EDGE",EDGE,{"disambiguationData":[OSD([sQuery(id+"F0.wireOp",EDGE,"E69.MirrorCS"),sQuery(id+"F0.wireOp",EDGE,"E70.MirrorCS")])]});
            var Q14;
            Q14=makeQuery(id+"F8.opExtrude","SWEPT_EDGE",EDGE,{"disambiguationData":[OSD([sQuery(id+"F0.wireOp",EDGE,"E59"),sQuery(id+"F0.wireOp",EDGE,"E60")])]});
            var Q15;
            Q15=makeQuery(id+"F8.opExtrude","SWEPT_EDGE",EDGE,{"disambiguationData":[OSD([sQuery(id+"F0.wireOp",EDGE,"E56"),sQuery(id+"F0.wireOp",EDGE,"E63")])]});
            fillet(context, id + "F22", {"entities" : qUnion([Q0, Q1, Q2, Q3, Q4, Q5, Q6, Q7, Q8, Q9, Q10, Q11, Q12, Q13, Q14, Q15]), "radius" : 1 * mm, "tangentPropagation" : true, "allowEdgeOverflow" : false});
        }
        {
            var Q0;
            Q0=makeQuery(id+"F8.opExtrude","CAP_EDGE",EDGE,{"disambiguationData":[OSD([sQuery(id+"F0.wireOp",EDGE,"E74.MirrorCS")])],"isStart":false});
            var Q1;
            Q1=makeQuery(id+"F8.opExtrude","CAP_EDGE",EDGE,{"disambiguationData":[OSD([sQuery(id+"F0.wireOp",EDGE,"E74.MirrorCS")])],"isStart":true});
            var Q2;
            Q2=makeQuery(id+"F8.opExtrude","CAP_EDGE",EDGE,{"disambiguationData":[OSD([sQuery(id+"F0.wireOp",EDGE,"E60")])],"isStart":true});
            var Q3;
            Q3=makeQuery(id+"F8.opExtrude","CAP_EDGE",EDGE,{"disambiguationData":[OSD([sQuery(id+"F0.wireOp",EDGE,"E59")])],"isStart":false});
            fillet(context, id + "F23", {"entities" : qUnion([Q0, Q1, Q2, Q3]), "radius" : 0.5 * mm, "tangentPropagation" : true, "allowEdgeOverflow" : false});
        }
        {
            var Q0;
            Q0=makeQuery(id+"F1.opExtrude","SWEPT_FACE",FACE,{"disambiguationData":[OSD([sQuery(id+"F0.wireOp",EDGE,"E2")])]});
            var Q1;
            {var subQ0=sQuery(id+"F0.wireOp",EDGE,"E9");var subQ1=sQuery(id+"F0.wireOp",EDGE,"E8");var subQ2=sQuery(id+"F0.wireOp",EDGE,"E3");Q1=makeQuery(id+"F2.boolean.opBoolean","MERGE",FACE,{"derivedFrom":[makeQuery(id+"F1.opExtrude","CAP_FACE",FACE,{"disambiguationData":[OSD([sQuery(id+"F0.wireOp",EDGE,"E0"),sQuery(id+"F0.wireOp",EDGE,"E1"),sQuery(id+"F0.wireOp",EDGE,"E2"),subQ2,subQ1,subQ0])],"isStart":false}),makeQuery(id+"F2.opExtrude","CAP_FACE",FACE,{"disambiguationData":[OSD([subQ2,sQuery(id+"F0.wireOp",EDGE,"E4"),sQuery(id+"F0.wireOp",EDGE,"E6"),sQuery(id+"F0.wireOp",EDGE,"E7"),subQ1,subQ0,sQuery(id+"F0.wireOp",EDGE,"E10"),sQuery(id+"F0.wireOp",EDGE,"E12"),sQuery(id+"F0.wireOp",EDGE,"E13"),sQuery(id+"F0.wireOp",EDGE,"E14"),sQuery(id+"F0.wireOp",EDGE,"E15"),sQuery(id+"F0.wireOp",EDGE,"E16"),sQuery(id+"F0.wireOp",EDGE,"E17")])],"isStart":false})]});}
            var Q2;
            Q2=makeQuery(id+"F1.opExtrude","SWEPT_FACE",FACE,{"disambiguationData":[OSD([sQuery(id+"F0.wireOp",EDGE,"E1")])]});
            var Q3;
            Q3=makeQuery(id+"F3.opExtrude","CAP_FACE",FACE,{"disambiguationData":[OSD([sQuery(id+"F0.wireOp",EDGE,"E3"),sQuery(id+"F0.wireOp",EDGE,"E4"),sQuery(id+"F0.wireOp",EDGE,"E6"),sQuery(id+"F0.wireOp",EDGE,"E7"),sQuery(id+"F0.wireOp",EDGE,"E8"),sQuery(id+"F0.wireOp",EDGE,"E9"),sQuery(id+"F0.wireOp",EDGE,"E10"),sQuery(id+"F0.wireOp",EDGE,"E12"),sQuery(id+"F0.wireOp",EDGE,"E13"),sQuery(id+"F0.wireOp",EDGE,"E14"),sQuery(id+"F0.wireOp",EDGE,"E15"),sQuery(id+"F0.wireOp",EDGE,"E16"),sQuery(id+"F0.wireOp",EDGE,"E17")])],"isStart":false});
            var Q4;
            Q4=makeQuery(id+"F1.opExtrude","SWEPT_FACE",FACE,{"disambiguationData":[OSD([sQuery(id+"F0.wireOp",EDGE,"E3")])]});
            var Q5;
            Q5=makeQuery(id+"F1.opExtrude","SWEPT_FACE",FACE,{"disambiguationData":[OSD([sQuery(id+"F0.wireOp",EDGE,"E0")])]});
            var Q6;
            Q6=makeQuery(id+"F1.opExtrude","SWEPT_FACE",FACE,{"disambiguationData":[OSD([sQuery(id+"F0.wireOp",EDGE,"E8")])]});
            var Q7;
            Q7=makeQuery(id+"F1.opExtrude","SWEPT_FACE",FACE,{"disambiguationData":[OSD([sQuery(id+"F0.wireOp",EDGE,"E9")])]});
            var Q8;
            Q8=makeQuery(id+"F2.opExtrude","CAP_FACE",FACE,{"disambiguationData":[OSD([sQuery(id+"F0.wireOp",EDGE,"E3"),sQuery(id+"F0.wireOp",EDGE,"E4"),sQuery(id+"F0.wireOp",EDGE,"E6"),sQuery(id+"F0.wireOp",EDGE,"E7"),sQuery(id+"F0.wireOp",EDGE,"E8"),sQuery(id+"F0.wireOp",EDGE,"E9"),sQuery(id+"F0.wireOp",EDGE,"E10"),sQuery(id+"F0.wireOp",EDGE,"E12"),sQuery(id+"F0.wireOp",EDGE,"E13"),sQuery(id+"F0.wireOp",EDGE,"E14"),sQuery(id+"F0.wireOp",EDGE,"E15"),sQuery(id+"F0.wireOp",EDGE,"E16"),sQuery(id+"F0.wireOp",EDGE,"E17")])],"isStart":true});
            var Q9;
            {var subQ0=sQuery(id+"F0.wireOp",EDGE,"E9");var subQ1=sQuery(id+"F0.wireOp",EDGE,"E8");var subQ2=sQuery(id+"F0.wireOp",EDGE,"E3");Q9=makeQuery(id+"F3.boolean.opBoolean","MERGE",FACE,{"derivedFrom":[makeQuery(id+"F1.opExtrude","CAP_FACE",FACE,{"disambiguationData":[OSD([sQuery(id+"F0.wireOp",EDGE,"E0"),sQuery(id+"F0.wireOp",EDGE,"E1"),sQuery(id+"F0.wireOp",EDGE,"E2"),subQ2,subQ1,subQ0])],"isStart":true}),makeQuery(id+"F3.opExtrude","CAP_FACE",FACE,{"disambiguationData":[OSD([subQ2,sQuery(id+"F0.wireOp",EDGE,"E4"),sQuery(id+"F0.wireOp",EDGE,"E6"),sQuery(id+"F0.wireOp",EDGE,"E7"),subQ1,subQ0,sQuery(id+"F0.wireOp",EDGE,"E10"),sQuery(id+"F0.wireOp",EDGE,"E12"),sQuery(id+"F0.wireOp",EDGE,"E13"),sQuery(id+"F0.wireOp",EDGE,"E14"),sQuery(id+"F0.wireOp",EDGE,"E15"),sQuery(id+"F0.wireOp",EDGE,"E16"),sQuery(id+"F0.wireOp",EDGE,"E17")])],"isStart":true})]});}
            fillet(context, id + "F24", {"entities" : qUnion([Q0, Q1, Q2, Q3, Q4, Q5, Q6, Q7, Q8, Q9]), "radius" : 0.5 * mm, "tangentPropagation" : true, "allowEdgeOverflow" : false});
        }
        {
            var Q0;
            Q0=makeQuery(id+"F13.opExtrude","CAP_FACE",FACE,{"disambiguationData":[OSD([sQuery(id+"F0.wireOp",EDGE,"E41.MirrorCS"),sQuery(id+"F0.wireOp",EDGE,"E44.MirrorCS"),sQuery(id+"F0.wireOp",EDGE,"E47.MirrorCS"),sQuery(id+"F0.wireOp",EDGE,"E49.MirrorC"),sQuery(id+"F0.wireOp",EDGE,"E55.MirrorC")])],"isStart":false});
            var Q1;
            Q1=makeQuery(id+"F18.opExtrude","CAP_FACE",FACE,{"disambiguationData":[OSD([sQuery(id+"F0.wireOp",EDGE,"E27.MirrorCS"),sQuery(id+"F0.wireOp",EDGE,"E28.MirrorCS"),sQuery(id+"F0.wireOp",EDGE,"E29.MirrorCS"),sQuery(id+"F0.wireOp",EDGE,"E38.MirrorC"),sQuery(id+"F0.wireOp",EDGE,"E39.MirrorC")])],"isStart":false});
            var Q2;
            {var subQ0=sQuery(id+"F0.wireOp",EDGE,"E29.MirrorCS");var subQ1=sQuery(id+"F0.wireOp",EDGE,"E28.MirrorCS");var subQ2=sQuery(id+"F0.wireOp",EDGE,"E27.MirrorCS");Q2=makeQuery(id+"F17.boolean.opBoolean","MERGE",FACE,{"derivedFrom":[makeQuery(id+"F16.opExtrude","CAP_FACE",FACE,{"disambiguationData":[OSD([sQuery(id+"F0.wireOp",EDGE,"E24.MirrorCS"),sQuery(id+"F0.wireOp",EDGE,"E25.MirrorCS"),sQuery(id+"F0.wireOp",EDGE,"E26.MirrorCS"),subQ2,subQ1,subQ0])],"isStart":false}),makeQuery(id+"F17.opExtrude","CAP_FACE",FACE,{"disambiguationData":[OSD([subQ2,subQ1,subQ0,sQuery(id+"F0.wireOp",EDGE,"E30.MirrorCS"),sQuery(id+"F0.wireOp",EDGE,"E31.MirrorCS"),sQuery(id+"F0.wireOp",EDGE,"E32.MirrorCS"),sQuery(id+"F0.wireOp",EDGE,"E33.MirrorC"),sQuery(id+"F0.wireOp",EDGE,"E34.MirrorC"),sQuery(id+"F0.wireOp",EDGE,"E35.MirrorC"),sQuery(id+"F0.wireOp",EDGE,"E36.MirrorC"),sQuery(id+"F0.wireOp",EDGE,"E37.MirrorC"),sQuery(id+"F0.wireOp",EDGE,"E38.MirrorC"),sQuery(id+"F0.wireOp",EDGE,"E39.MirrorC")])],"isStart":false})]});}
            var Q3;
            {var subQ0=sQuery(id+"F0.wireOp",EDGE,"E47.MirrorCS");var subQ1=sQuery(id+"F0.wireOp",EDGE,"E44.MirrorCS");var subQ2=sQuery(id+"F0.wireOp",EDGE,"E41.MirrorCS");Q3=makeQuery(id+"F12.boolean.opBoolean","MERGE",FACE,{"derivedFrom":[makeQuery(id+"F11.opExtrude","CAP_FACE",FACE,{"disambiguationData":[OSD([sQuery(id+"F0.wireOp",EDGE,"E40.MirrorCS"),subQ2,sQuery(id+"F0.wireOp",EDGE,"E43.MirrorCS"),subQ1,subQ0,sQuery(id+"F0.wireOp",EDGE,"E48.MirrorCS")])],"isStart":false}),makeQuery(id+"F12.opExtrude","CAP_FACE",FACE,{"disambiguationData":[OSD([subQ2,sQuery(id+"F0.wireOp",EDGE,"E42.MirrorCS"),subQ1,sQuery(id+"F0.wireOp",EDGE,"E45.MirrorCS"),sQuery(id+"F0.wireOp",EDGE,"E46.MirrorCS"),subQ0,sQuery(id+"F0.wireOp",EDGE,"E49.MirrorC"),sQuery(id+"F0.wireOp",EDGE,"E50.MirrorC"),sQuery(id+"F0.wireOp",EDGE,"E51.MirrorC"),sQuery(id+"F0.wireOp",EDGE,"E52.MirrorC"),sQuery(id+"F0.wireOp",EDGE,"E53.MirrorC"),sQuery(id+"F0.wireOp",EDGE,"E54.MirrorC"),sQuery(id+"F0.wireOp",EDGE,"E55.MirrorC")])],"isStart":false})]});}
            var Q4;
            Q4=makeQuery(id+"F11.opExtrude","SWEPT_FACE",FACE,{"disambiguationData":[OSD([sQuery(id+"F0.wireOp",EDGE,"E48.MirrorCS")])]});
            var Q5;
            Q5=makeQuery(id+"F16.opExtrude","SWEPT_FACE",FACE,{"disambiguationData":[OSD([sQuery(id+"F0.wireOp",EDGE,"E25.MirrorCS")])]});
            var Q6;
            Q6=makeQuery(id+"F16.opExtrude","SWEPT_FACE",FACE,{"disambiguationData":[OSD([sQuery(id+"F0.wireOp",EDGE,"E26.MirrorCS")])]});
            var Q7;
            Q7=makeQuery(id+"F11.opExtrude","SWEPT_FACE",FACE,{"disambiguationData":[OSD([sQuery(id+"F0.wireOp",EDGE,"E40.MirrorCS")])]});
            var Q8;
            Q8=makeQuery(id+"F11.opExtrude","SWEPT_FACE",FACE,{"disambiguationData":[OSD([sQuery(id+"F0.wireOp",EDGE,"E41.MirrorCS")])]});
            var Q9;
            Q9=makeQuery(id+"F16.opExtrude","SWEPT_FACE",FACE,{"disambiguationData":[OSD([sQuery(id+"F0.wireOp",EDGE,"E29.MirrorCS")])]});
            var Q10;
            {var subQ0=sQuery(id+"F0.wireOp",EDGE,"E29.MirrorCS");var subQ1=sQuery(id+"F0.wireOp",EDGE,"E28.MirrorCS");var subQ2=sQuery(id+"F0.wireOp",EDGE,"E27.MirrorCS");Q10=makeQuery(id+"F18.boolean.opBoolean","MERGE",FACE,{"derivedFrom":[makeQuery(id+"F16.opExtrude","CAP_FACE",FACE,{"disambiguationData":[OSD([sQuery(id+"F0.wireOp",EDGE,"E24.MirrorCS"),sQuery(id+"F0.wireOp",EDGE,"E25.MirrorCS"),sQuery(id+"F0.wireOp",EDGE,"E26.MirrorCS"),subQ2,subQ1,subQ0])],"isStart":true}),makeQuery(id+"F18.opExtrude","CAP_FACE",FACE,{"disambiguationData":[OSD([subQ2,subQ1,subQ0,sQuery(id+"F0.wireOp",EDGE,"E38.MirrorC"),sQuery(id+"F0.wireOp",EDGE,"E39.MirrorC")])],"isStart":true})]});}
            var Q11;
            {var subQ0=sQuery(id+"F0.wireOp",EDGE,"E47.MirrorCS");var subQ1=sQuery(id+"F0.wireOp",EDGE,"E44.MirrorCS");var subQ2=sQuery(id+"F0.wireOp",EDGE,"E41.MirrorCS");Q11=makeQuery(id+"F13.boolean.opBoolean","MERGE",FACE,{"derivedFrom":[makeQuery(id+"F11.opExtrude","CAP_FACE",FACE,{"disambiguationData":[OSD([sQuery(id+"F0.wireOp",EDGE,"E40.MirrorCS"),subQ2,sQuery(id+"F0.wireOp",EDGE,"E43.MirrorCS"),subQ1,subQ0,sQuery(id+"F0.wireOp",EDGE,"E48.MirrorCS")])],"isStart":true}),makeQuery(id+"F13.opExtrude","CAP_FACE",FACE,{"disambiguationData":[OSD([subQ2,subQ1,subQ0,sQuery(id+"F0.wireOp",EDGE,"E49.MirrorC"),sQuery(id+"F0.wireOp",EDGE,"E55.MirrorC")])],"isStart":true})]});}
            var Q12;
            Q12=makeQuery(id+"F11.opExtrude","SWEPT_FACE",FACE,{"disambiguationData":[OSD([sQuery(id+"F0.wireOp",EDGE,"E43.MirrorCS")])]});
            var Q13;
            Q13=makeQuery(id+"F12.opExtrude","CAP_FACE",FACE,{"disambiguationData":[OSD([sQuery(id+"F0.wireOp",EDGE,"E41.MirrorCS"),sQuery(id+"F0.wireOp",EDGE,"E42.MirrorCS"),sQuery(id+"F0.wireOp",EDGE,"E44.MirrorCS"),sQuery(id+"F0.wireOp",EDGE,"E45.MirrorCS"),sQuery(id+"F0.wireOp",EDGE,"E46.MirrorCS"),sQuery(id+"F0.wireOp",EDGE,"E47.MirrorCS"),sQuery(id+"F0.wireOp",EDGE,"E49.MirrorC"),sQuery(id+"F0.wireOp",EDGE,"E50.MirrorC"),sQuery(id+"F0.wireOp",EDGE,"E51.MirrorC"),sQuery(id+"F0.wireOp",EDGE,"E52.MirrorC"),sQuery(id+"F0.wireOp",EDGE,"E53.MirrorC"),sQuery(id+"F0.wireOp",EDGE,"E54.MirrorC"),sQuery(id+"F0.wireOp",EDGE,"E55.MirrorC")])],"isStart":true});
            var Q14;
            Q14=makeQuery(id+"F16.opExtrude","SWEPT_FACE",FACE,{"disambiguationData":[OSD([sQuery(id+"F0.wireOp",EDGE,"E25.MirrorCS")])]});
            var Q15;
            Q15=makeQuery(id+"F17.opExtrude","CAP_FACE",FACE,{"disambiguationData":[OSD([sQuery(id+"F0.wireOp",EDGE,"E27.MirrorCS"),sQuery(id+"F0.wireOp",EDGE,"E28.MirrorCS"),sQuery(id+"F0.wireOp",EDGE,"E29.MirrorCS"),sQuery(id+"F0.wireOp",EDGE,"E30.MirrorCS"),sQuery(id+"F0.wireOp",EDGE,"E31.MirrorCS"),sQuery(id+"F0.wireOp",EDGE,"E32.MirrorCS"),sQuery(id+"F0.wireOp",EDGE,"E33.MirrorC"),sQuery(id+"F0.wireOp",EDGE,"E34.MirrorC"),sQuery(id+"F0.wireOp",EDGE,"E35.MirrorC"),sQuery(id+"F0.wireOp",EDGE,"E36.MirrorC"),sQuery(id+"F0.wireOp",EDGE,"E37.MirrorC"),sQuery(id+"F0.wireOp",EDGE,"E38.MirrorC"),sQuery(id+"F0.wireOp",EDGE,"E39.MirrorC")])],"isStart":true});
            var Q16;
            Q16=makeQuery(id+"F16.opExtrude","SWEPT_FACE",FACE,{"disambiguationData":[OSD([sQuery(id+"F0.wireOp",EDGE,"E24.MirrorCS")])]});
            var Q17;
            Q17=makeQuery(id+"F11.opExtrude","SWEPT_FACE",FACE,{"disambiguationData":[OSD([sQuery(id+"F0.wireOp",EDGE,"E44.MirrorCS")])]});
            fillet(context, id + "F25", {"entities" : qUnion([Q0, Q1, Q2, Q3, Q4, Q5, Q6, Q7, Q8, Q9, Q10, Q11, Q12, Q13, Q14, Q15, Q16, Q17]), "radius" : 0.5 * mm, "tangentPropagation" : true, "allowEdgeOverflow" : false});
        }
    });
